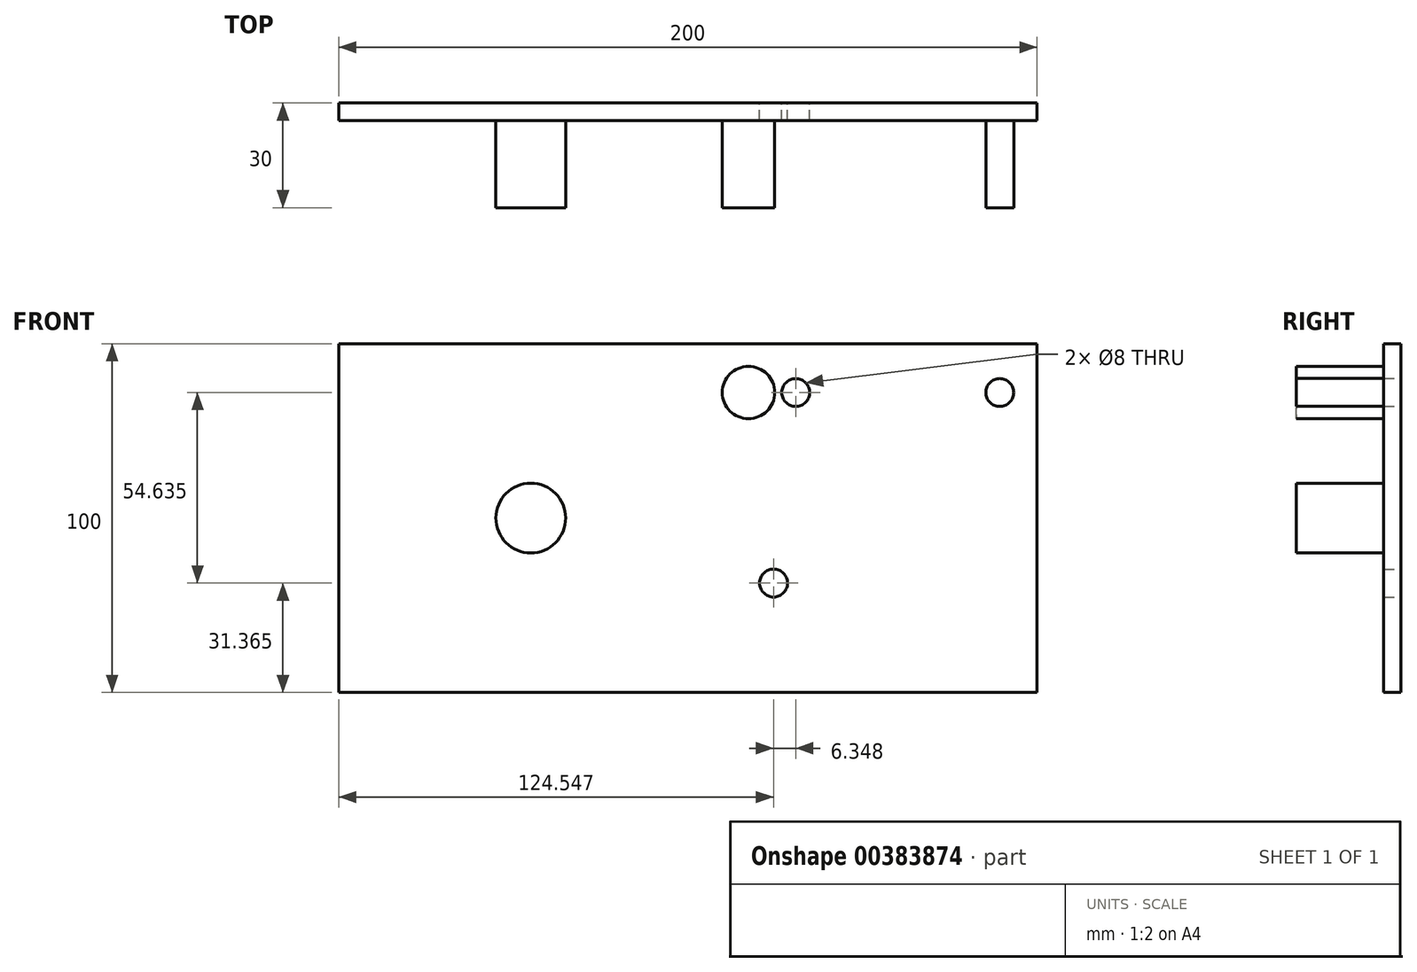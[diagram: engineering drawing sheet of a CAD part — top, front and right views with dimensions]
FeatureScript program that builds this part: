
annotation { "Feature Type Name" : "Feature", "Feature Type Description" : "" }
export const myFeature = defineFeature(function(context is Context, id is Id, definition is map)
    precondition{}
    {
        {
            var Q0;
            Q0=qCreatedBy(makeId("Front.planeOp"),FACE);
            var sketch = newSketch(context, id + "F0", { "sketchPlane" : qUnion([Q0])});
            skLineSegment(sketch, "E0.bottom", {"start": v(100, -50) * mm, "end": v(-100, -50) * mm});
            skLineSegment(sketch, "E0.top", {"start": v(100, 50) * mm, "end": v(-100, 50) * mm});
            skLineSegment(sketch, "E0.left", {"start": v(100, -50) * mm, "end": v(100, 50) * mm});
            skLineSegment(sketch, "E0.right", {"start": v(-100, -50) * mm, "end": v(-100, 50) * mm});
            skPoint(sketch, "E0.middle", {"position": v(0, 0) * mm});
            skLineSegment(sketch, "E1", {"start": v(0, 0) * mm, "end": v(-45, 0) * mm, "construction": true});
            skLineSegment(sketch, "E2", {"start": v(-45, 0) * mm, "end": v(17.35, 36) * mm, "construction": true});
            skLineSegment(sketch, "E3", {"start": v(-45, 0) * mm, "end": v(24.55, -18.63) * mm, "construction": true});
            skCircle(sketch, "E4", {"center": v(17.35, 36) * mm, "radius": 7.5 * mm});
            skCircle(sketch, "E5", {"center": v(24.55, -18.63) * mm, "radius": 4 * mm});
            skCircle(sketch, "E6", {"center": v(-45, 0) * mm, "radius": 10 * mm, "construction": true});
            skLineSegment(sketch, "E7", {"start": v(17.35, 36) * mm, "end": v(128.3, 36) * mm, "construction": true});
            skLineSegment(sketch, "E8", {"start": v(-45, 0) * mm, "end": v(30.9, 36) * mm, "construction": true});
            skCircle(sketch, "E9", {"center": v(30.9, 36) * mm, "radius": 4 * mm});
            skLineSegment(sketch, "E10", {"start": v(17.35, 36) * mm, "end": v(89.35, 36) * mm, "construction": true});
            skCircle(sketch, "E11", {"center": v(89.35, 36) * mm, "radius": 4 * mm});
            skSolve(sketch);
        }
        {
            var Q0;
            Q0 = qSketchRegion(id + "F0", true);
            extrude(context, id + "F1", {"entities" : qUnion([Q0]), "depth" : 5 * mm});
        }
        {
            var Q0;
            Q0=qCreatedBy(makeId("Front.planeOp"),FACE);
            var sketch = newSketch(context, id + "F2", { "sketchPlane" : qUnion([Q0])});
            skLineSegment(sketch, "E12", {"start": v(0, 0) * mm, "end": v(-45, 0) * mm, "construction": true});
            skLineSegment(sketch, "E13", {"start": v(-45, 0) * mm, "end": v(17.35, 36) * mm, "construction": true});
            skLineSegment(sketch, "E14", {"start": v(-45, 0) * mm, "end": v(24.55, -18.63) * mm, "construction": true});
            skCircle(sketch, "E15", {"center": v(-45, 0) * mm, "radius": 10 * mm});
            skCircle(sketch, "E16", {"center": v(17.35, 36) * mm, "radius": 7.5 * mm});
            skLineSegment(sketch, "E17", {"start": v(17.35, 36) * mm, "end": v(89.35, 36) * mm});
            skCircle(sketch, "E18", {"center": v(89.35, 36) * mm, "radius": 4 * mm});
            skSolve(sketch);
        }
        {
            var Q0;
            Q0 = qSketchRegion(id + "F2", true);
            extrude(context, id + "F3", {"entities" : qUnion([Q0]), "operationType" : NewBodyOperationType.ADD, "depth" : 30 * mm});
        }
    });
